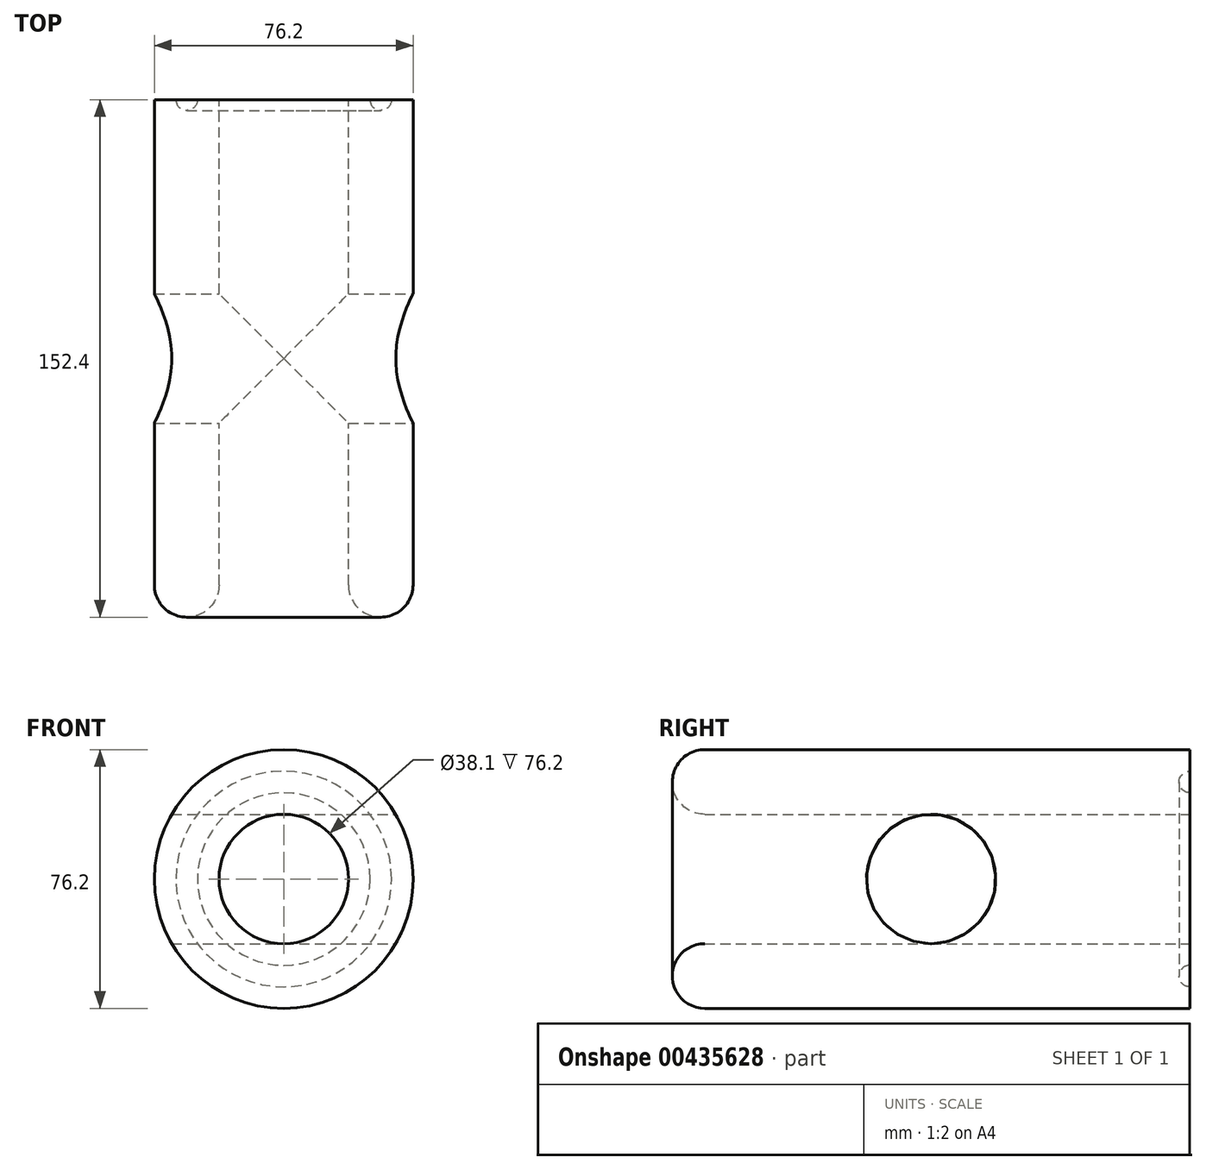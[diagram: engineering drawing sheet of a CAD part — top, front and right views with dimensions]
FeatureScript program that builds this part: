
annotation { "Feature Type Name" : "Feature", "Feature Type Description" : "" }
export const myFeature = defineFeature(function(context is Context, id is Id, definition is map)
    precondition{}
    {
        {
            var Q0;
            Q0=qCreatedBy(makeId("Front.planeOp"),FACE);
            var sketch = newSketch(context, id + "F0", { "sketchPlane" : qUnion([Q0])});
            skCircle(sketch, "E0", {"center": v(0, 0) * mm, "radius": 38.1 * mm});
            skCircle(sketch, "E1", {"center": v(0, 0) * mm, "radius": 19.05 * mm});
            skSolve(sketch);
        }
        {
            var Q0;
            Q0=makeQuery(id+"F0.imprint","IMPRINT",FACE,{"disambiguationData":[TD([[makeQuery(id+"F0.imprint","IMPRINT",EDGE,{"derivedFrom":sQuery(id+"F0.wireOp",EDGE,"E0")}),1.0]])]});
            extrude(context, id + "F1", {"entities" : qUnion([Q0]), "endBound" : BoundingType.SYMMETRIC, "depth" : 152.4 * mm});
        }
        {
            var Q0;
            Q0=makeQuery(id+"F1.opExtrude","CAP_EDGE",EDGE,{"disambiguationData":[OSD([sQuery(id+"F0.wireOp",EDGE,"E0")])],"isStart":false});
            var Q1;
            Q1=makeQuery(id+"F1.opExtrude","CAP_EDGE",EDGE,{"disambiguationData":[OSD([sQuery(id+"F0.wireOp",EDGE,"E1")])],"isStart":false});
            fillet(context, id + "F2", {"entities" : qUnion([Q0, Q1]), "radius" : 9.52 * mm, "tangentPropagation" : true, "allowEdgeOverflow" : false});
        }
        {
            var Q0;
            Q0=makeQuery(id+"F1.opExtrude","CAP_FACE",FACE,{"disambiguationData":[OSD([sQuery(id+"F0.wireOp",EDGE,"E0"),sQuery(id+"F0.wireOp",EDGE,"E1")])],"isStart":true});
            cPlane(context, id + "F3", {"entities" : qUnion([Q0]), "cplaneType" : CPlaneType.OFFSET, "offset" : 0 * mm, "width" : 152.4 * mm, "height" : 152.4 * mm});
        }
        {
            var Q0;
            Q0=qCreatedBy(id+"F3.planeOp",FACE);
            var sketch = newSketch(context, id + "F4", { "sketchPlane" : qUnion([Q0])});
            skCircle(sketch, "E2", {"center": v(0, 0) * mm, "radius": 31.75 * mm});
            skCircle(sketch, "E3", {"center": v(0, 0) * mm, "radius": 25.4 * mm});
            skSolve(sketch);
        }
        {
            var Q0;
            Q0 = qSketchRegion(id + "F4", true);
            extrude(context, id + "F5", {"entities" : qUnion([Q0]), "operationType" : NewBodyOperationType.REMOVE, "oppositeDirection" : true, "depth" : 3.17 * mm});
        }
        {
            var Q0;
            Q0=makeQuery(id+"F5.boolean.opBoolean","COPY",EDGE,{"derivedFrom":makeQuery(id+"F5.opExtrude","CAP_EDGE",EDGE,{"disambiguationData":[OSD([sQuery(id+"F4.wireOp",EDGE,"E2")])],"isStart":false})});
            var Q1;
            Q1=makeQuery(id+"F5.boolean.opBoolean","COPY",EDGE,{"derivedFrom":makeQuery(id+"F5.opExtrude","CAP_EDGE",EDGE,{"disambiguationData":[OSD([sQuery(id+"F4.wireOp",EDGE,"E3")])],"isStart":false})});
            fillet(context, id + "F6", {"entities" : qUnion([Q0, Q1]), "radius" : 3.17 * mm, "tangentPropagation" : true, "allowEdgeOverflow" : false});
        }
        {
            var Q0;
            Q0=qCreatedBy(makeId("Right.planeOp"),FACE);
            cPlane(context, id + "F7", {"entities" : qUnion([Q0]), "cplaneType" : CPlaneType.OFFSET, "offset" : 76.2 * mm, "width" : 152.4 * mm, "height" : 152.4 * mm});
        }
        {
            var Q0;
            Q0=qCreatedBy(id+"F7.planeOp",FACE);
            var sketch = newSketch(context, id + "F8", { "sketchPlane" : qUnion([Q0])});
            skCircle(sketch, "E4", {"center": v(0, 0) * mm, "radius": 19.05 * mm});
            skSolve(sketch);
        }
        {
            var Q0;
            Q0 = qSketchRegion(id + "F8", true);
            extrude(context, id + "F9", {"entities" : qUnion([Q0]), "operationType" : NewBodyOperationType.REMOVE, "oppositeDirection" : true, "depth" : 152.4 * mm});
        }
    });
